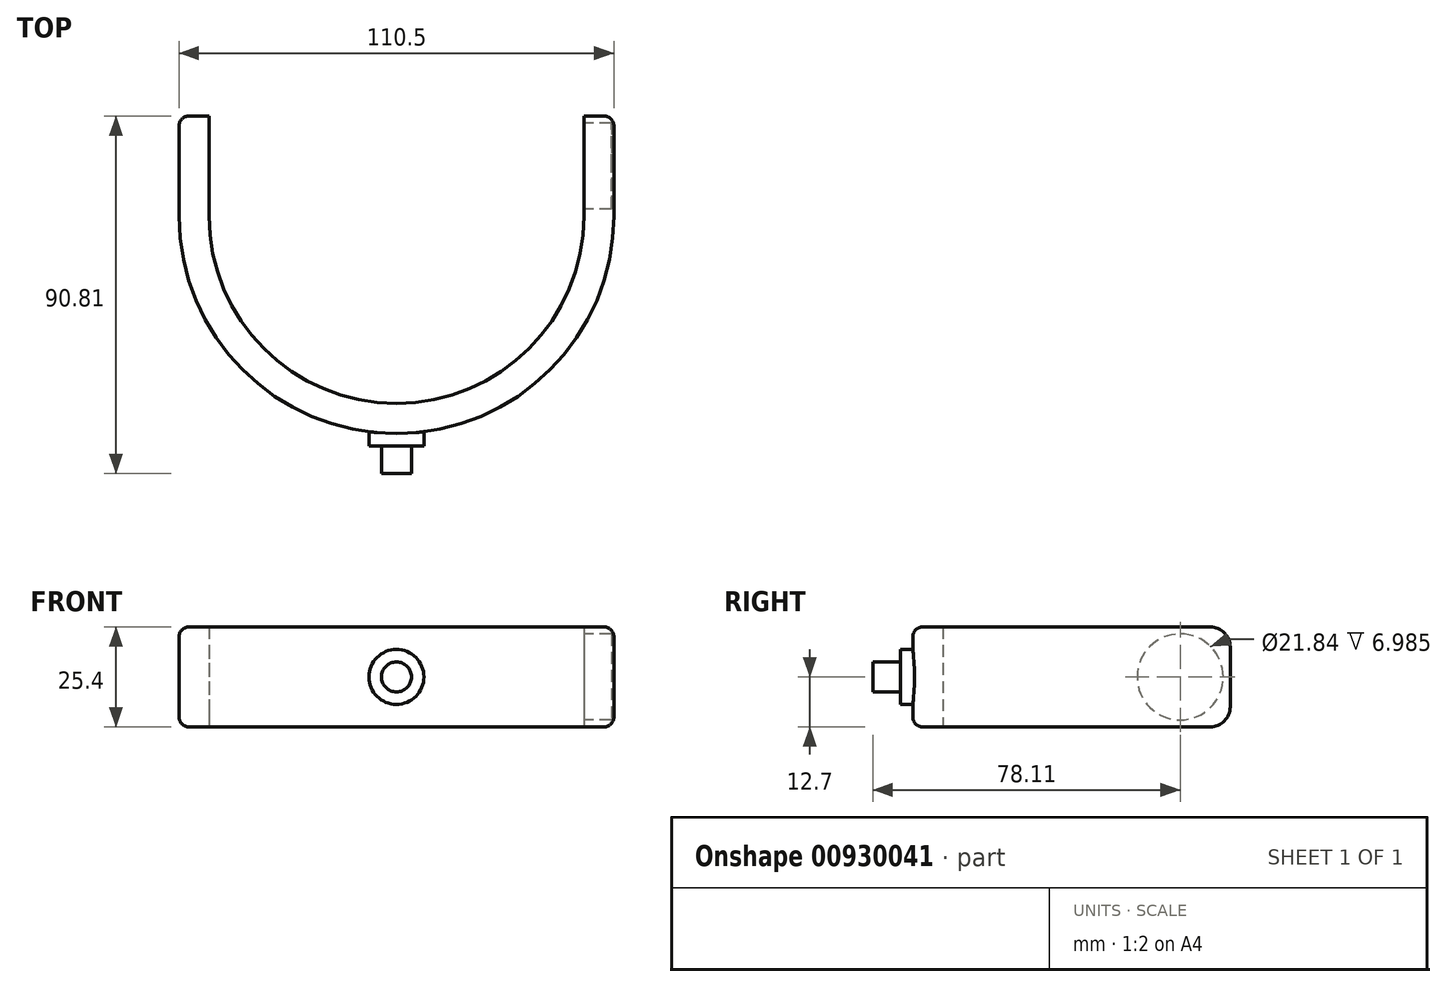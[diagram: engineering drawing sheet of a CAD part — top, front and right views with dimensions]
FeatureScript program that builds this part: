
annotation { "Feature Type Name" : "Feature", "Feature Type Description" : "" }
export const myFeature = defineFeature(function(context is Context, id is Id, definition is map)
    precondition{}
    {
        {
            var Q0;
            Q0=qCreatedBy(makeId("Top.planeOp"),FACE);
            var sketch = newSketch(context, id + "F0", { "sketchPlane" : qUnion([Q0])});
            skArc(sketch, "E0", {"start": v(47.63, 0) * mm, "mid": v(0, -47.63) * mm, "end": v(-47.63, 0) * mm});
            skArc(sketch, "E1", {"start": v(-55.25, 0) * mm, "mid": v(0, -55.25) * mm, "end": v(55.25, 0) * mm});
            skLineSegment(sketch, "E2.bottom", {"start": v(-55.25, 0) * mm, "end": v(-47.63, 0) * mm});
            skLineSegment(sketch, "E2.top", {"start": v(-55.25, 25.4) * mm, "end": v(-47.63, 25.4) * mm});
            skLineSegment(sketch, "E2.left", {"start": v(-55.25, 0) * mm, "end": v(-55.25, 25.4) * mm});
            skLineSegment(sketch, "E2.right", {"start": v(-47.62, 0) * mm, "end": v(-47.63, 25.4) * mm});
            skLineSegment(sketch, "E3.bottom", {"start": v(47.63, 0) * mm, "end": v(55.25, 0) * mm});
            skLineSegment(sketch, "E3.top", {"start": v(47.62, 25.4) * mm, "end": v(55.25, 25.4) * mm});
            skLineSegment(sketch, "E3.left", {"start": v(47.62, 0) * mm, "end": v(47.62, 25.4) * mm});
            skLineSegment(sketch, "E3.right", {"start": v(55.25, 0) * mm, "end": v(55.25, 25.4) * mm});
            skSolve(sketch);
        }
        {
            var Q0;
            Q0 = qSketchRegion(id + "F0", true);
            extrude(context, id + "F1", {"entities" : qUnion([Q0]), "depth" : 25.4 * mm, "offsetDistance" : 25.4 * mm});
        }
        {
            var Q0;
            Q0=makeQuery(id+"F1.opExtrude","CAP_EDGE",EDGE,{"disambiguationData":[OSD([sQuery(id+"F0.wireOp",EDGE,"E1")])],"isStart":true});
            cPoint(context, id + "F2", {"entities" : qUnion([Q0]), "parameter" : 0.5});
        }
        {
            var Q0;
            Q0=qCreatedBy(makeId("Front.planeOp"),FACE);
            var Q1;
            Q1 = qCreatedBy(id + "F2" ,VERTEX);
            cPlane(context, id + "F3", {"entities" : qUnion([Q0, Q1]), "cplaneType" : CPlaneType.PLANE_POINT, "offset" : 25.4 * mm, "width" : 152.4 * mm, "height" : 152.4 * mm});
        }
        {
            var Q0;
            Q0=qCreatedBy(id+"F3.planeOp",FACE);
            var sketch = newSketch(context, id + "F4", { "sketchPlane" : qUnion([Q0])});
            skPoint(sketch, "E4", {"position": v(0, 0) * mm});
            skPoint(sketch, "E5", {"position": v(0, 25.4) * mm});
            skLineSegment(sketch, "E6", {"start": v(0, 25.4) * mm, "end": v(0, 0) * mm, "construction": true});
            skCircle(sketch, "E7", {"center": v(0, 12.7) * mm, "radius": 3.81 * mm});
            skCircle(sketch, "E8", {"center": v(0, 12.7) * mm, "radius": 6.99 * mm});
            skSolve(sketch);
        }
        {
            var Q0;
            Q0=makeQuery(id+"F1.opExtrude","SWEPT_FACE",FACE,{"disambiguationData":[OSD([sQuery(id+"F0.wireOp",EDGE,"E3.left")])]});
            var sketch = newSketch(context, id + "F5", { "sketchPlane" : qUnion([Q0])});
            skCircle(sketch, "E9", {"center": v(-12.7, 12.7) * mm, "radius": 10.92 * mm});
            skPoint(sketch, "E9.centerSnap0", {"position": v(-12.7, 0) * mm});
            skPoint(sketch, "E9.centerSnap1", {"position": v(-25.4, 12.7) * mm});
            skSolve(sketch);
        }
        {
            var Q0;
            Q0 = qSketchRegion(id + "F5", true);
            extrude(context, id + "F6", {"entities" : qUnion([Q0]), "operationType" : NewBodyOperationType.REMOVE, "oppositeDirection" : true, "depth" : 7 * mm, "offsetDistance" : 25.4 * mm});
        }
        {
            var Q0;
            Q0 = qSketchRegion(id + "F4", true);
            extrude(context, id + "F7", {"entities" : qUnion([Q0]), "operationType" : NewBodyOperationType.ADD, "depth" : 3.17 * mm, "offsetDistance" : 25.4 * mm, "hasSecondDirection" : true, "secondDirectionOppositeDirection" : true, "secondDirectionDepth" : 3.17 * mm});
        }
        {
            var Q0;
            Q0=makeQuery(id+"F4.imprint","IMPRINT",FACE,{"disambiguationData":[TD([[makeQuery(id+"F4.imprint","IMPRINT",EDGE,{"derivedFrom":sQuery(id+"F4.wireOp",EDGE,"E7")}),1.0]])]});
            extrude(context, id + "F8", {"entities" : qUnion([Q0]), "operationType" : NewBodyOperationType.ADD, "depth" : 10.16 * mm, "offsetDistance" : 25.4 * mm, "hasSecondDirection" : true, "secondDirectionOppositeDirection" : true, "secondDirectionDepth" : 3.17 * mm});
        }
        {
            var Q0;
            Q0=makeQuery(id+"F1.opExtrude","CAP_EDGE",EDGE,{"disambiguationData":[OSD([sQuery(id+"F0.wireOp",EDGE,"E2.top")])],"isStart":true});
            var Q1;
            Q1=makeQuery(id+"F1.opExtrude","CAP_EDGE",EDGE,{"disambiguationData":[OSD([sQuery(id+"F0.wireOp",EDGE,"E2.top")])],"isStart":false});
            var Q2;
            Q2=makeQuery(id+"F1.opExtrude","CAP_EDGE",EDGE,{"disambiguationData":[OSD([sQuery(id+"F0.wireOp",EDGE,"E3.top")])],"isStart":false});
            var Q3;
            Q3=makeQuery(id+"F1.opExtrude","CAP_EDGE",EDGE,{"disambiguationData":[OSD([sQuery(id+"F0.wireOp",EDGE,"E3.top")])],"isStart":true});
            fillet(context, id + "F9", {"entities" : qUnion([Q0, Q1, Q2, Q3]), "radius" : 5.08 * mm, "tangentPropagation" : true, "allowEdgeOverflow" : false});
        }
        {
            var Q0;
            Q0=makeQuery(id+"F1.opExtrude","CAP_EDGE",EDGE,{"disambiguationData":[OSD([sQuery(id+"F0.wireOp",EDGE,"E1")])],"isStart":true});
            fillet(context, id + "F10", {"entities" : qUnion([Q0]), "radius" : 2.54 * mm, "tangentPropagation" : true, "allowEdgeOverflow" : false});
        }
    });
